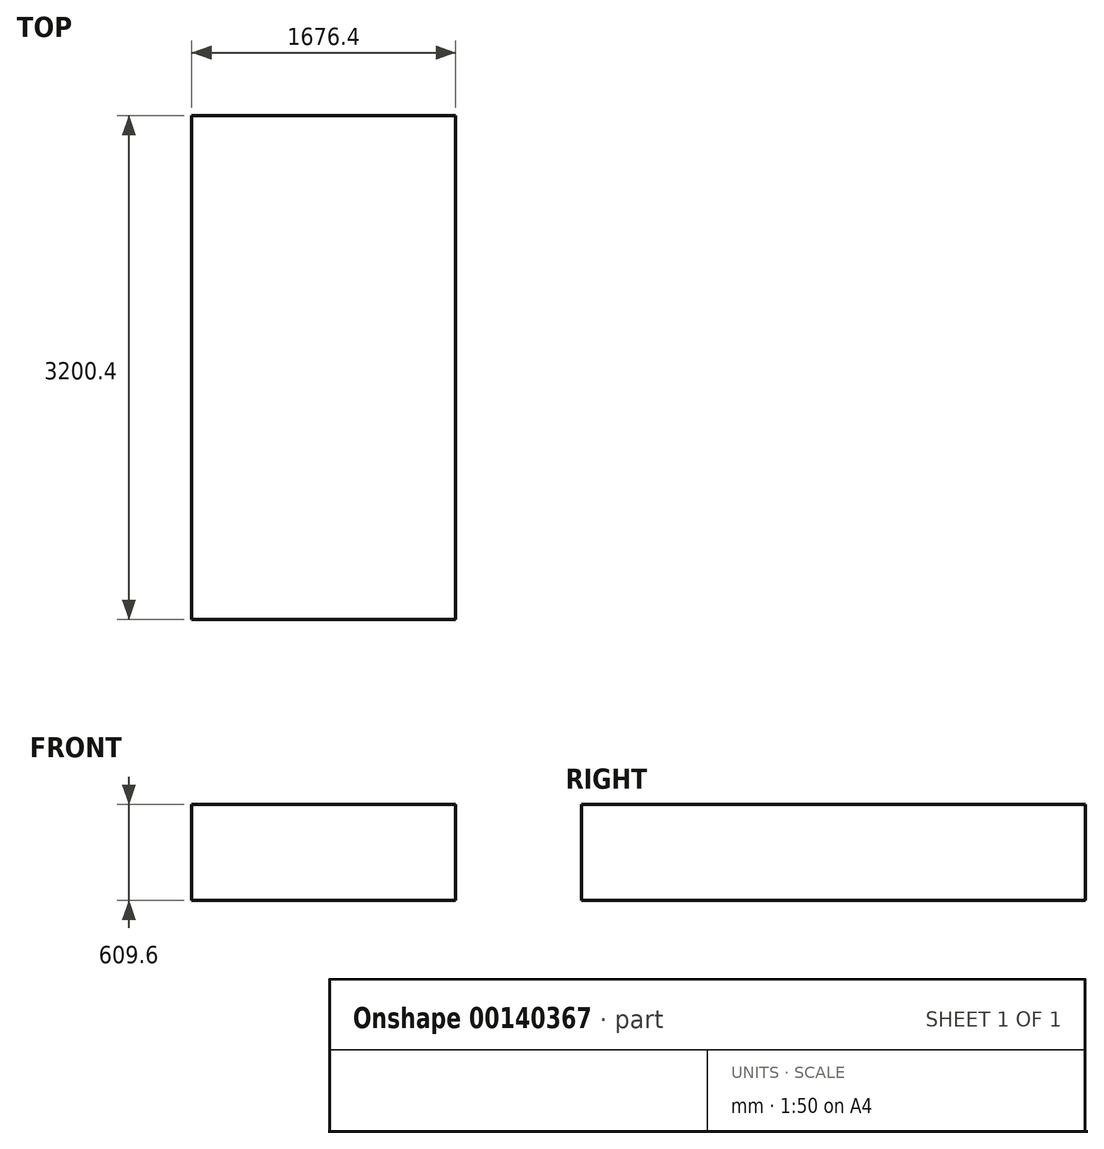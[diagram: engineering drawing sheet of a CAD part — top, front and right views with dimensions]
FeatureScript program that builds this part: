
annotation { "Feature Type Name" : "Feature", "Feature Type Description" : "" }
export const myFeature = defineFeature(function(context is Context, id is Id, definition is map)
    precondition{}
    {
        {
            var Q0;
            Q0=qCreatedBy(makeId("Front.planeOp"),FACE);
            var sketch = newSketch(context, id + "F0", { "sketchPlane" : qUnion([Q0])});
            skLineSegment(sketch, "E0.bottom", {"start": v(0, 0) * mm, "end": v(1676.4, 0) * mm});
            skLineSegment(sketch, "E0.top", {"start": v(0, 609.6) * mm, "end": v(1676.4, 609.6) * mm});
            skLineSegment(sketch, "E0.left", {"start": v(0, 0) * mm, "end": v(0, 609.6) * mm});
            skLineSegment(sketch, "E0.right", {"start": v(1676.4, 0) * mm, "end": v(1676.4, 609.6) * mm});
            skSolve(sketch);
        }
        {
            var Q0;
            Q0 = qSketchRegion(id + "F0", true);
            extrude(context, id + "F1", {"entities" : qUnion([Q0]), "depth" : 3200.4 * mm});
        }
    });
